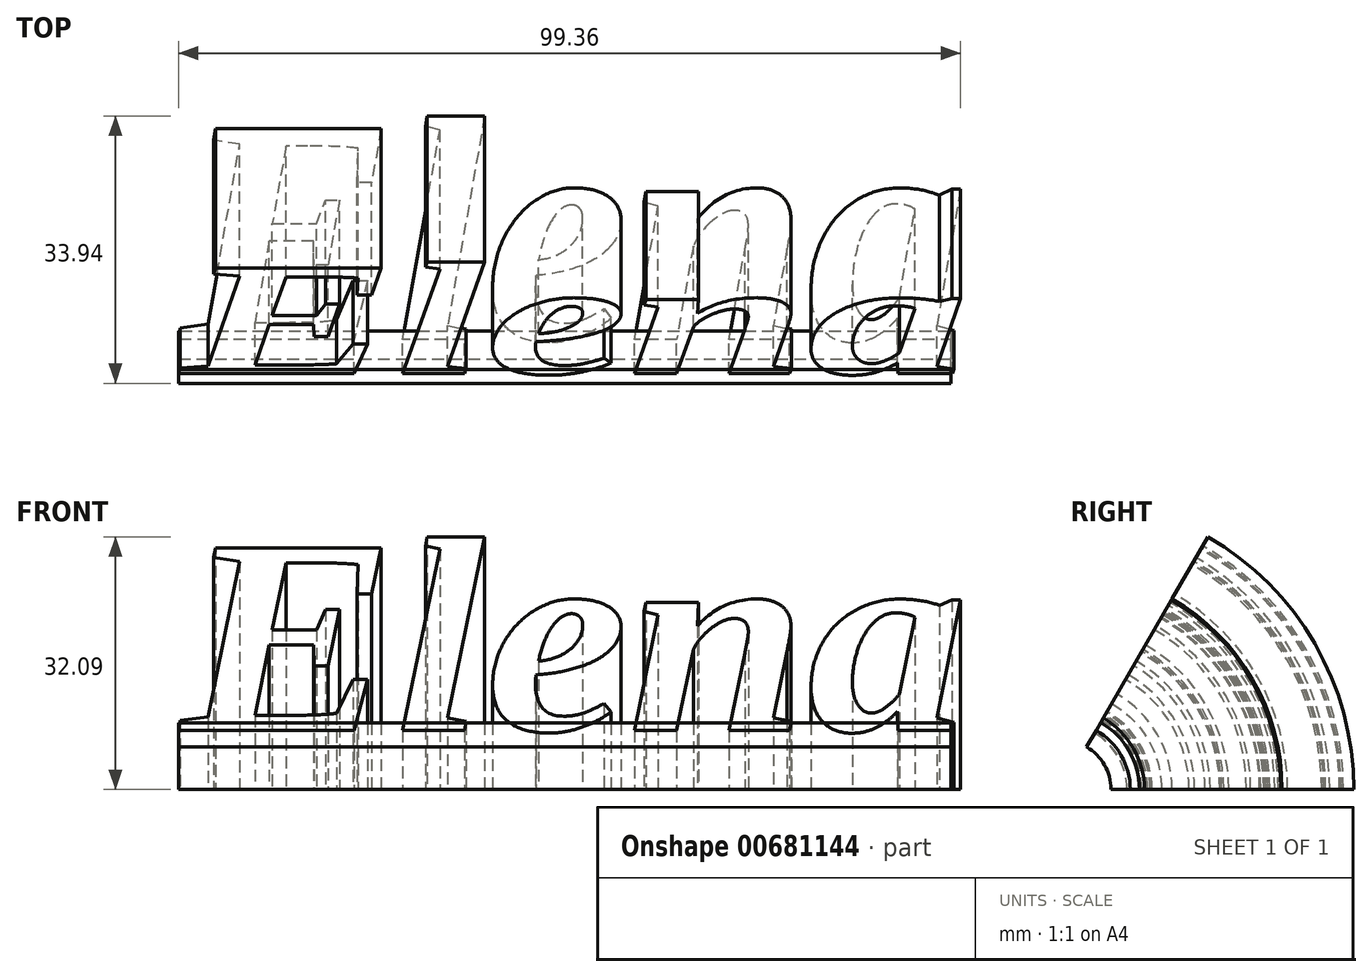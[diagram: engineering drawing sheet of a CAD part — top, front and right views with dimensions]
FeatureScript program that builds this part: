
annotation { "Feature Type Name" : "Feature", "Feature Type Description" : "" }
export const myFeature = defineFeature(function(context is Context, id is Id, definition is map)
    precondition{}
    {
        {
            var Q0;
            Q0=qCreatedBy(makeId("Top.planeOp"),FACE);
            var sketch = newSketch(context, id + "F0", { "sketchPlane" : qUnion([Q0])});
            skText(sketch, "E0", { "text": "Elena", "fontName": "Tinos-BoldItalic.ttf"});
            const initialGuessF0  = {"E0": [-0.07643, -0.0129, 1, 0, 0.02946]};
            skSetInitialGuess(sketch, initialGuessF0);
            skSolve(sketch);
        }
        {
            var Q0;
            Q0=qCreatedBy(makeId("Top.planeOp"),FACE);
            var sketch = newSketch(context, id + "F1", { "sketchPlane" : qUnion([Q0])});
            skLineSegment(sketch, "E1.bottom", {"start": v(-76.7, -11.83) * mm, "end": v(21.42, -11.83) * mm});
            skLineSegment(sketch, "E1.top", {"start": v(-76.7, -15.34) * mm, "end": v(21.42, -15.34) * mm});
            skLineSegment(sketch, "E1.left", {"start": v(-76.7, -11.83) * mm, "end": v(-76.7, -15.34) * mm});
            skLineSegment(sketch, "E1.right", {"start": v(21.42, -11.83) * mm, "end": v(21.42, -15.34) * mm});
            skSolve(sketch);
        }
        {
            var Q0;
            Q0=qCreatedBy(makeId("Top.planeOp"),FACE);
            var sketch = newSketch(context, id + "F2", { "sketchPlane" : qUnion([Q0])});
            skLineSegment(sketch, "E2", {"start": v(-82.65, -21.56) * mm, "end": v(29, -21.56) * mm});
            skSolve(sketch);
        }
        {
            var Q0;
            Q0 = qSketchRegion(id + "F0", true);
            var Q1;
            Q1=makeQuery(id+"F1.imprint","IMPRINT",FACE,{"disambiguationData":[TD([[makeQuery(id+"F1.imprint","IMPRINT",EDGE,{"derivedFrom":sQuery(id+"F1.wireOp",EDGE,"E1.bottom")}),-1.0]])]});
            var Q2;
            Q2=sQuery(id+"F2.wireOp",EDGE,"E2");
            revolve(context, id + "F3", {"entities" : qUnion([Q0, Q1]), "axis" : qUnion([Q2]), "revolveType" : RevolveType.ONE_DIRECTION, "angle" : 60 * degree});
        }
    });
